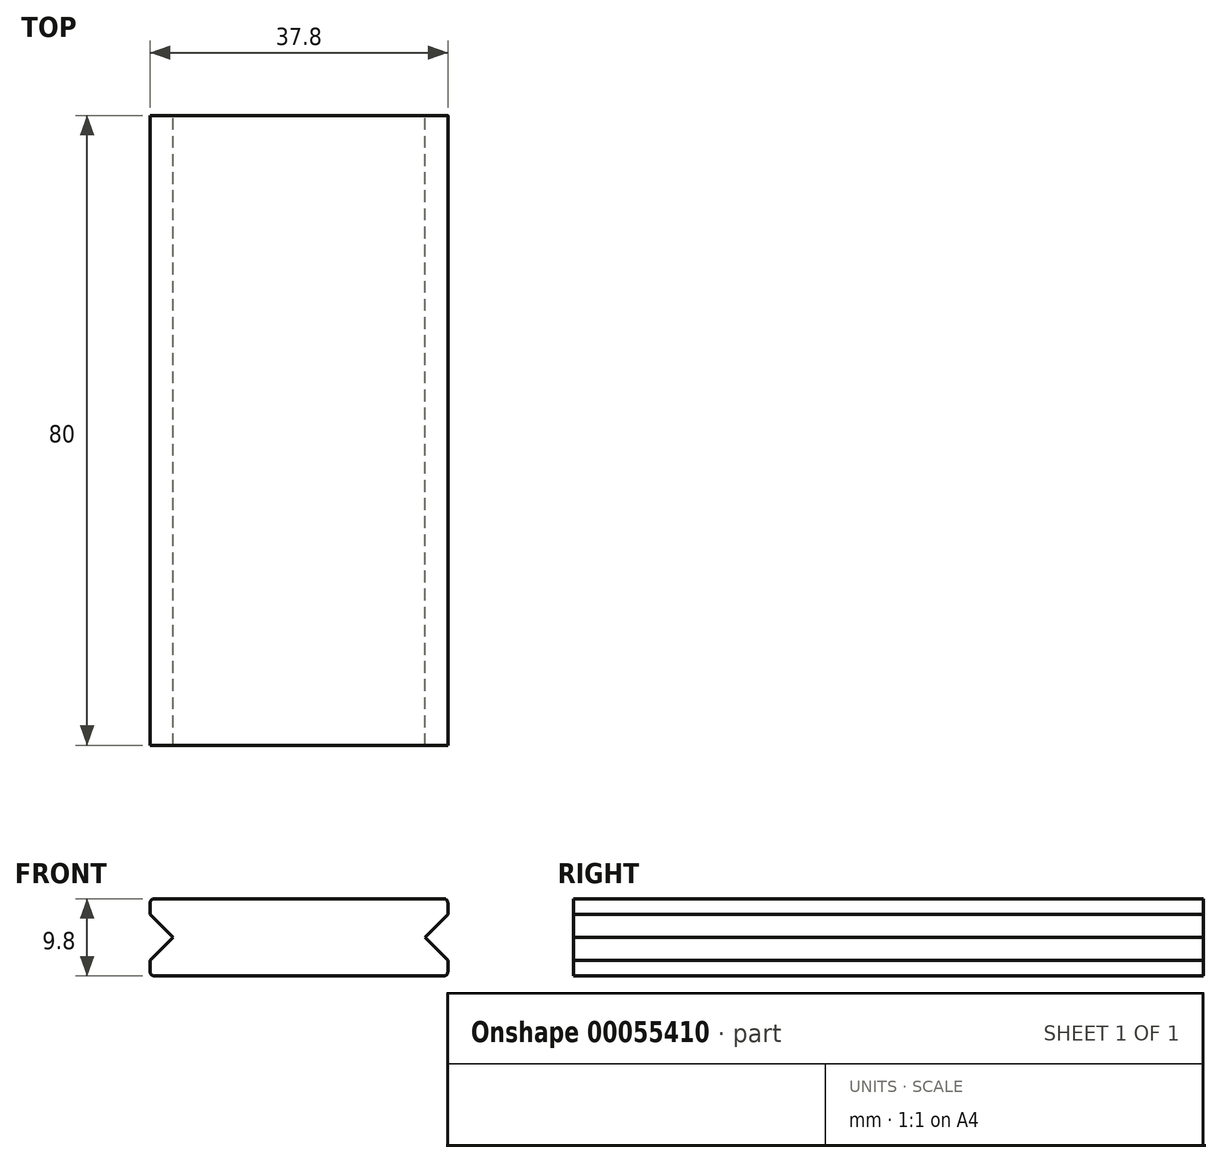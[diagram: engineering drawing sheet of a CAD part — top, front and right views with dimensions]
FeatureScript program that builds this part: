
annotation { "Feature Type Name" : "Feature", "Feature Type Description" : "" }
export const myFeature = defineFeature(function(context is Context, id is Id, definition is map)
    precondition{}
    {
        {
            var Q0;
            Q0=qCreatedBy(makeId("Front.planeOp"),FACE);
            var sketch = newSketch(context, id + "F0", { "sketchPlane" : qUnion([Q0])});
            skLineSegment(sketch, "E0", {"start": v(0, 4.9) * mm, "end": v(-18.4, 4.9) * mm});
            skLineSegment(sketch, "E1", {"start": v(-18.9, 4.4) * mm, "end": v(-18.9, 2.9) * mm});
            skLineSegment(sketch, "E2", {"start": v(-18.9, 2.9) * mm, "end": v(-16, 0) * mm});
            skPoint(sketch, "E3.visualSharp", {"position": v(-18.9, 4.9) * mm});
            skArc(sketch, "E3.filletArc", {"start": v(-18.4, 4.9) * mm, "mid": v(-18.75, 4.75) * mm, "end": v(-18.9, 4.4) * mm});
            skArc(sketch, "E4.MirrorCS", {"start": v(18.4, 4.9) * mm, "mid": v(18.75, 4.75) * mm, "end": v(18.9, 4.4) * mm});
            skLineSegment(sketch, "E5.MirrorCS", {"start": v(18.9, 4.4) * mm, "end": v(18.9, 2.9) * mm});
            skLineSegment(sketch, "E6.MirrorCS", {"start": v(0, 4.9) * mm, "end": v(18.4, 4.9) * mm});
            skLineSegment(sketch, "E7.MirrorCS", {"start": v(18.9, 2.9) * mm, "end": v(16, 0) * mm});
            skPoint(sketch, "E8.MirrorP", {"position": v(18.9, 4.9) * mm});
            skArc(sketch, "E9.MirrorCS", {"start": v(18.4, -4.9) * mm, "mid": v(18.75, -4.75) * mm, "end": v(18.9, -4.4) * mm});
            skArc(sketch, "E10.MirrorCS", {"start": v(-18.4, -4.9) * mm, "mid": v(-18.75, -4.75) * mm, "end": v(-18.9, -4.4) * mm});
            skLineSegment(sketch, "E11.MirrorCS", {"start": v(18.9, -4.4) * mm, "end": v(18.9, -2.9) * mm});
            skLineSegment(sketch, "E12.MirrorCS", {"start": v(-18.9, -4.4) * mm, "end": v(-18.9, -2.9) * mm});
            skLineSegment(sketch, "E13.MirrorCS", {"start": v(-18.9, -2.9) * mm, "end": v(-16, 0) * mm});
            skLineSegment(sketch, "E14.MirrorCS", {"start": v(0, -4.9) * mm, "end": v(-18.4, -4.9) * mm});
            skPoint(sketch, "E15.MirrorP", {"position": v(18.9, -4.9) * mm});
            skPoint(sketch, "E16.MirrorP", {"position": v(-18.9, -4.9) * mm});
            skLineSegment(sketch, "E17.MirrorCS", {"start": v(18.9, -2.9) * mm, "end": v(16, 0) * mm});
            skLineSegment(sketch, "E18.MirrorCS", {"start": v(0, -4.9) * mm, "end": v(18.4, -4.9) * mm});
            skSolve(sketch);
        }
        {
            var Q0;
            Q0=qSketchRegion(id+"F0",true);
            extrude(context, id + "F1", {"entities" : qUnion([Q0]), "depth" : 40 * mm, "hasSecondDirection" : true, "secondDirectionOppositeDirection" : true, "secondDirectionDepth" : 40 * mm});
        }
    });
